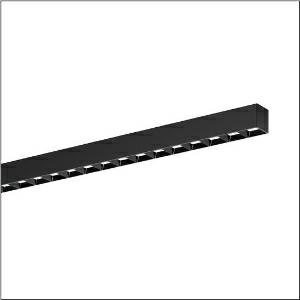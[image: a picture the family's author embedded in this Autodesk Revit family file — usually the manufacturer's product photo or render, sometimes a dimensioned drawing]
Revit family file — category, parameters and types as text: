
# Revit family: silica_r__21_51mx21dc4abb_1522
name_source: partatom
category: Lighting Fixtures
units: mm (PartAtom-declared; Revit-internal decimal feet)

## family parameters
Cut with Voids When Loaded = No
Host = Face
Light Source = No
Part Type = Normal
Room Calculation Point = No
Round Connector Dimension = Use Diameter
Shared = No

## types (1)
- --- (1 x LED, 10800 lm, 64.8 W, 4000K)
    Apparent Load = 65 VA
    CIE Flux Codes = 87 99 100 100 100
    Color Rendering = 80
    Color Temperature = 4000K
    Default Elevation = 1800 mm
    Description = Silica® 21, office luminaire, primary light control with darklight reflector, of PMMA, black, CAT 2 (L<= 3000cd/m²), light emission: direct distribution, primary light characteristic: symmetric, installation type: surface-mounted, LED, rated luminous flux: 10.800lm, luminous efficacy: 167lm/W, light colour: 840, colour temperature: 4000K, control gear: DALI 2, with terminal, 3+2-pole, max. 2.5mm², mains connection: 220..240V, AC, 50/60Hz, rated input power: 64.8W, luminaire housing, of aluminium, matt jet black (RAL 9005), length: 3.004mm, width: 53mm, height: 53mm, protection rating (complete): IP20, insulation class (complete): insulation class I (protective earthing), certification: CE, permissible operating ambient temperature: 0..+35°C, standard: EN 50419, packaging unit: 1 piece
    Height = 53 mm
    Lamp = 1 x LED
    Lamp Light Flux = 10800 lm
    Lamp Power = 64.8 W
    Lamp count = 1
    Length = 3004 mm
    Luminous efficacy = 167 lm/W
    Manufacturer = Siteco
    ModVariant = No
    Model = 51MX21DC4ABB
    Mounting Place = Ceiling
    Mounting Type = Surface mounted
    Number of Poles = 1
    OnlyDefault = Yes
    Power Factor = 1
    Product Name = Silica® 21
    Product group = office luminaire | ceiling mounted
    ProductGroupID = 302
    Protection Class = Protection class I
    Protection Degree = IP 20
    RLX_Detail_Level = 1
    RLX_Emergency_Light_Flux = 0 lm
    RLX_Emergency_Type = 0
    RLX_Emergency_Type_DB = No
    RlxData = <blob elided: 64145 chars, md5=a9a88270>
    Socket = socket
    Standby Power = 0 W
    System Light Flux = 10800 lm
    System Power = 65 W
    Type Comments = factory setting: luminous flux: 100 % | dim-lin: 254 | 367 mA
    Type Image = l_1335908.jpg
    URL = http://relux.com
    VarID = @adj_123706
    Voltage = 0 V
    Weight = 0.00 kg
    Width = 53 mm

## geometry (parser evidence)
native form markers: Blend x4, Sweep x11
no freeform markers — native parametric forms only
